# Revit family: HXSM
name_source: partatom
category: Mechanical Equipment
units: mm (PartAtom-declared; Revit-internal decimal feet)

## family parameters
Always vertical = Yes
Cut with Voids When Loaded = No
Part Type = Normal
Room Calculation Point = No
Round Connector Dimension = Use Diameter
Shared = No
Work Plane-Based = No

## types (8) — shared parameters
0 = 0"
1" = 1"
1.5 = 1 1/2"
2" = 2"
2' = 24"
4" = 4"
Manufacturer = Loren Cook Company
Model = HXSM
ONE EIGTH = 1/8"
Type Comments = Hooded Supply Ventilator Medium-Pressure Steel Propeller Roof Mounted/Belt Drive
URL = www.lorencook.com

## per-type parameters (varying)
| type | (A-C)/2 | (T_SQ/2)+.125" | (T_SQ/2)-2" | -(A/2) | -(C/2) | -L/2 | A | A-1.5" | A-C | A/2 | B | B-.125" | B/2 | C | C/2 | L | L/2 | RO | RO/2 | T_SQ | T_SQ/2 | W | W/2 |
| 20-HXSM | 8 5/8" | 16 1/8" | 14" | -13 5/8" | -5" | -26" | 27 1/4" | 25 3/4" | 17 1/4" | 13 5/8" | 2" | 1 7/8" | 1" | 10" | 5" | 52" | 26" | 27 1/2" | 13 3/4" | 32" | 16" | 52" | 26" |
| 30-HXSM | 10 1/4" | 21 1/8" | 19" | -15 1/4" | -5" | -34 1/2" | 30 1/2" | 29" | 20 1/2" | 15 1/4" | 3" | 2 7/8" | 1 1/2" | 10" | 5" | 69" | 34 1/2" | 37 1/2" | 18 3/4" | 42" | 21" | 69" | 34 1/2" |
| 36-HXSM | 11 1/2" | 24 1/8" | 22" | -16 1/2" | -5" | -40" | 33" | 31 1/2" | 23" | 16 1/2" | 3" | 2 7/8" | 1 1/2" | 10" | 5" | 80" | 40" | 43 1/2" | 21 3/4" | 48" | 24" | 80" | 40" |
| 42-HXSM | 14" | 27 1/8" | 25" | -19" | -5" | -45" | 38" | 36 1/2" | 28" | 19" | 3" | 2 7/8" | 1 1/2" | 10" | 5" | 90" | 45" | 49 1/2" | 24 3/4" | 54" | 27" | 90" | 45" |
| 48-HXSM | 14" | 30 1/8" | 28" | -20 3/4" | -6 3/4" | -55" | 41 1/2" | 40" | 28" | 20 3/4" | 3" | 2 7/8" | 1 1/2" | 13 1/2" | 6 3/4" | 110" | 55" | 55 1/2" | 27 3/4" | 60" | 30" | 90" | 45" |
| 54-HXSM | 14 7/8" | 33 1/8" | 31" | -22 1/4" | -7 3/8" | -55 1/2" | 44 1/2" | 43" | 29 3/4" | 22 1/4" | 3" | 2 7/8" | 1 1/2" | 14 3/4" | 7 3/8" | 111" | 55 1/2" | 61 1/2" | 30 3/4" | 66" | 33" | 109" | 54 1/2" |
| 60-HXSM | 14 7/8" | 36 1/8" | 34" | -22 1/4" | -7 3/8" | -60 1/2" | 44 1/2" | 43" | 29 3/4" | 22 1/4" | 3" | 2 7/8" | 1 1/2" | 14 3/4" | 7 3/8" | 121" | 60 1/2" | 67 1/2" | 33 3/4" | 72" | 36" | 119" | 59 1/2" |
| 24-HXSM | 9 3/8" | 18 1/8" | 16" | -14 3/8" | -5" | -29 1/2" | 28 3/4" | 27 1/4" | 18 3/4" | 14 3/8" | 3" | 2 7/8" | 1 1/2" | 10" | 5" | 59" | 29 1/2" | 31 1/2" | 15 3/4" | 36" | 18" | 59" | 29 1/2" |

## geometry (parser evidence)
native form markers: Sweep x2
no freeform markers — native parametric forms only
